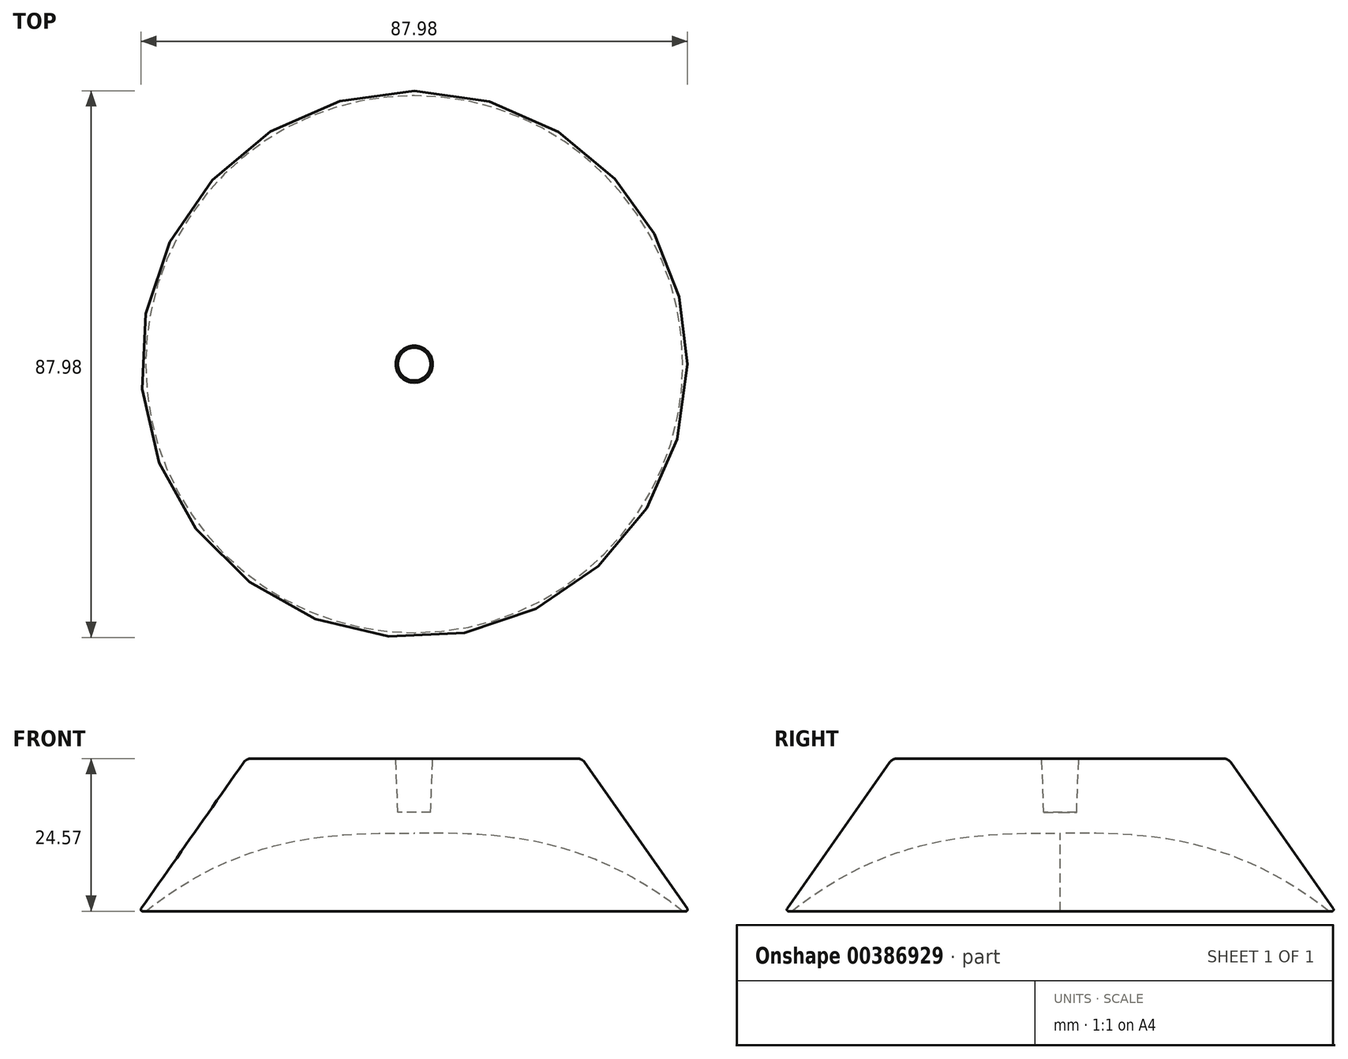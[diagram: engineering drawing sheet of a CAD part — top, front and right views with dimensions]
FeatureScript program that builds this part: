
annotation { "Feature Type Name" : "Feature", "Feature Type Description" : "" }
export const myFeature = defineFeature(function(context is Context, id is Id, definition is map)
    precondition{}
    {
        {
            var Q0;
            Q0=qCreatedBy(makeId("Front.planeOp"),FACE);
            var sketch = newSketch(context, id + "F0", { "sketchPlane" : qUnion([Q0])});
            skLineSegment(sketch, "E0", {"start": v(0, 0) * mm, "end": v(0, -10.87) * mm, "construction": true});
            skLineSegment(sketch, "E1", {"start": v(2.97, 12) * mm, "end": v(27.02, 12) * mm});
            skPoint(sketch, "E2.third.point", {"position": v(-55.87, -80.33) * mm});
            skLineSegment(sketch, "E3", {"start": v(0, 0) * mm, "end": v(0, 3.31) * mm});
            skLineSegment(sketch, "E4", {"start": v(43.23, -12.57) * mm, "end": v(44.23, -12.57) * mm});
            skLineSegment(sketch, "E5", {"start": v(44.23, -12.57) * mm, "end": v(27.02, 12) * mm});
            skLineSegment(sketch, "E6", {"start": v(0, 3.31) * mm, "end": v(2.64, 3.31) * mm});
            skLineSegment(sketch, "E7", {"start": v(2.64, 3.31) * mm, "end": v(2.97, 12) * mm});
            skPoint(sketch, "E8.orphan", {"position": v(0, 12) * mm});
            skFitSpline(sketch, "E9", {"points": [v(43.23, -12.57) * mm, v(0, 0) * mm], "startDerivative": vector(-47.87, 37.72) * mm, "endDerivative": vector(-38.7, 0) * mm});
            skSolve(sketch);
        }
        {
            var Q0;
            Q0=makeQuery(id+"F0.imprint","IMPRINT",FACE,{"disambiguationData":[TD([[makeQuery(id+"F0.imprint","IMPRINT",EDGE,{"derivedFrom":sQuery(id+"F0.wireOp",EDGE,"E1")}),-1.0]])]});
            var Q1;
            Q1=sQuery(id+"F0.wireOp",EDGE,"E0");
            revolve(context, id + "F1", {"surfaceOperationType" : NewSurfaceOperationType.NEW, "entities" : qUnion([Q0]), "axis" : qUnion([Q1]), "revolveType" : RevolveType.FULL});
        }
        {
            var Q0;
            Q0=makeQuery(id+"F1.opRevolve","SWEPT_EDGE",EDGE,{"disambiguationData":[OSD([sQuery(id+"F0.wireOp",EDGE,"E1"),sQuery(id+"F0.wireOp",EDGE,"E5")])]});
            fillet(context, id + "F2", {"entities" : qUnion([Q0]), "radius" : 1.5 * mm, "tangentPropagation" : true, "allowEdgeOverflow" : false});
        }
        {
            var Q0;
            Q0=makeQuery(id+"F1.opRevolve","SWEPT_EDGE",EDGE,{"disambiguationData":[OSD([sQuery(id+"F0.wireOp",EDGE,"E4"),sQuery(id+"F0.wireOp",EDGE,"E5")])]});
            fillet(context, id + "F3", {"entities" : qUnion([Q0]), "radius" : .25 * mm, "tangentPropagation" : true, "allowEdgeOverflow" : false});
        }
    });
